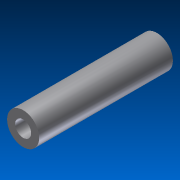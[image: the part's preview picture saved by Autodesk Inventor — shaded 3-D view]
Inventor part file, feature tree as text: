
AUTODESK INVENTOR PART (.ipt)
format: ipt  version: 2012 (Build 160160000, 160)  size: 78,336 bytes
history: native  units: in
note: dims shown in document units (in); Inventor stores cm internally (conversion verified against a paired STEP export)
features: extrude x1, sketch x1
ambient origin geometry x8: Origin, YZ Plane, XZ Plane, XY Plane, X Axis, Y Axis, Z Axis, Center Point
bodies: Solid1 (feature_tree)
feature tree (2):
  extrude  "Extrusion1"  Depth=0.2362in
  sketch  "Sketch1"  dims[d0=0.1181in d1=0.2362in d2=0.9843in d3=0.0in]
